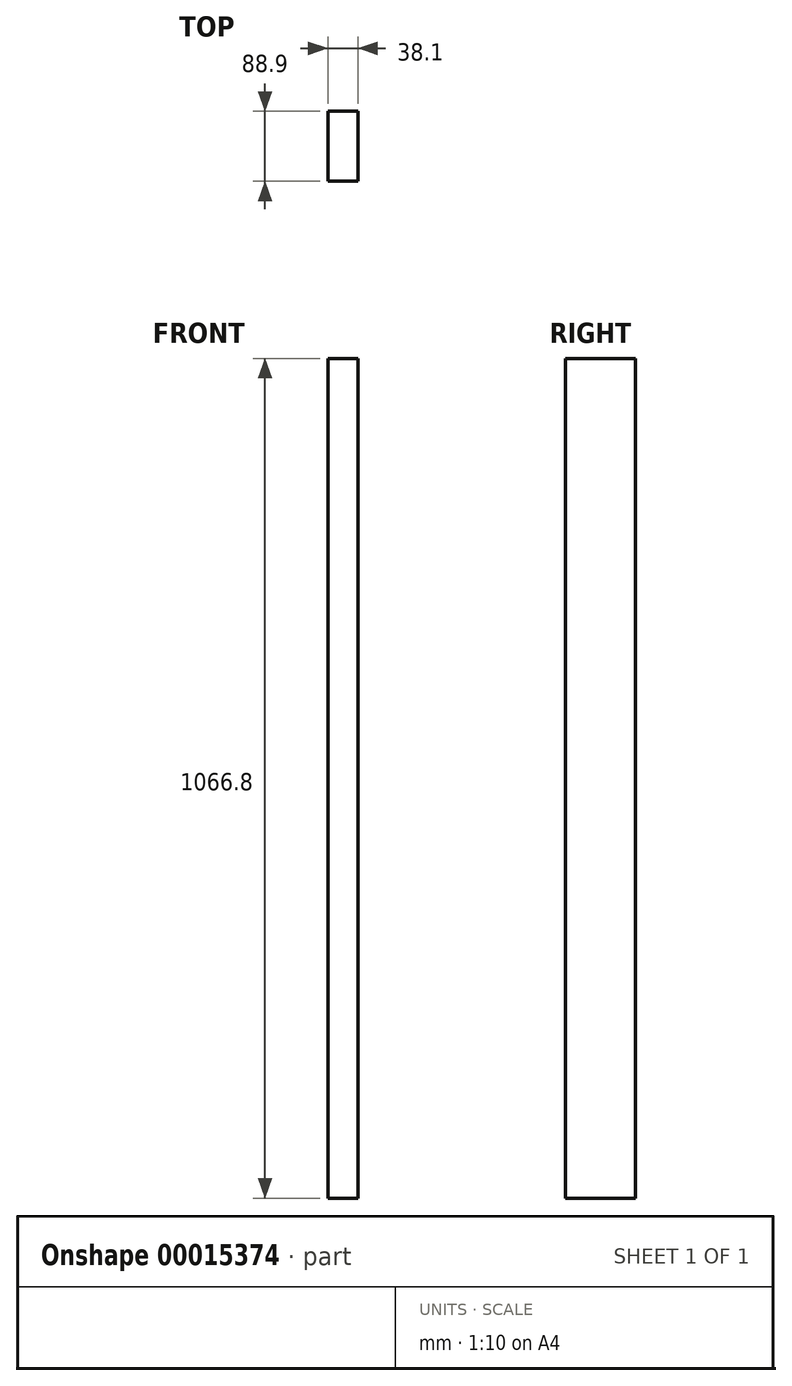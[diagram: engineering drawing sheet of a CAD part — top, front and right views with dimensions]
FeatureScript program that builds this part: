
annotation { "Feature Type Name" : "Feature", "Feature Type Description" : "" }
export const myFeature = defineFeature(function(context is Context, id is Id, definition is map)
    precondition{}
    {
        {
            var Q0;
            Q0=qCreatedBy(makeId("Top.planeOp"),FACE);
            var sketch = newSketch(context, id + "F0", { "sketchPlane" : qUnion([Q0])});
            skLineSegment(sketch, "E0.bottom", {"start": v(0, 0) * mm, "end": v(38.1, 0) * mm});
            skLineSegment(sketch, "E0.top", {"start": v(0, 88.9) * mm, "end": v(38.1, 88.9) * mm});
            skLineSegment(sketch, "E0.left", {"start": v(0, 0) * mm, "end": v(0, 88.9) * mm});
            skLineSegment(sketch, "E0.right", {"start": v(38.1, 0) * mm, "end": v(38.1, 88.9) * mm});
            skSolve(sketch);
        }
        {
            var Q0;
            Q0=makeQuery(id+"F0.imprint","IMPRINT",FACE,{"disambiguationData":[TD([[makeQuery(id+"F0.imprint","IMPRINT",EDGE,{"derivedFrom":sQuery(id+"F0.wireOp",EDGE,"E0.bottom")}),1.0]])]});
            extrude(context, id + "F1", {"entities" : qUnion([Q0]), "depth" : 1066.8 * mm});
        }
    });
